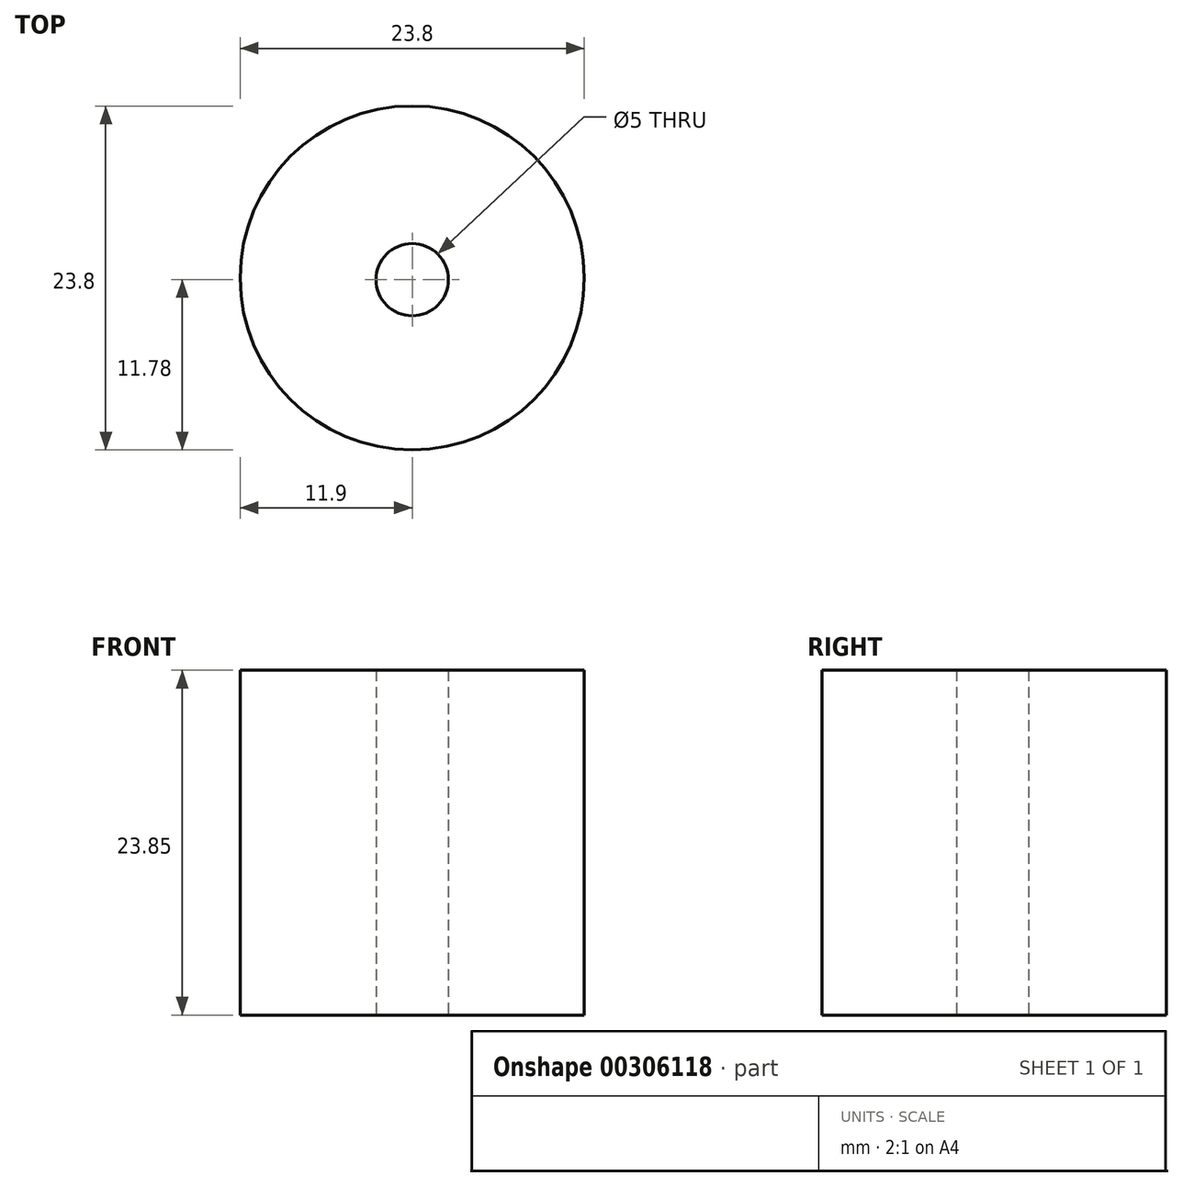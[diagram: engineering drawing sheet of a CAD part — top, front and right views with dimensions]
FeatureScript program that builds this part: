
annotation { "Feature Type Name" : "Feature", "Feature Type Description" : "" }
export const myFeature = defineFeature(function(context is Context, id is Id, definition is map)
    precondition{}
    {
        {
            var Q0;
            Q0=qCreatedBy(makeId("Top.planeOp"),FACE);
            var sketch = newSketch(context, id + "F0", { "sketchPlane" : qUnion([Q0])});
            skCircle(sketch, "E0", {"center": v(0, 0) * mm, "radius": 11.9 * mm});
            skCircle(sketch, "E1", {"center": v(0, -0.12) * mm, "radius": 2.5 * mm});
            skSolve(sketch);
        }
        {
            var Q0;
            Q0=makeQuery(id+"F0.imprint","IMPRINT",FACE,{"disambiguationData":[TD([[makeQuery(id+"F0.imprint","IMPRINT",EDGE,{"derivedFrom":sQuery(id+"F0.wireOp",EDGE,"E0")}),1.0]])]});
            extrude(context, id + "F1", {"entities" : qUnion([Q0]), "depth" : 23.85 * mm});
        }
    });
